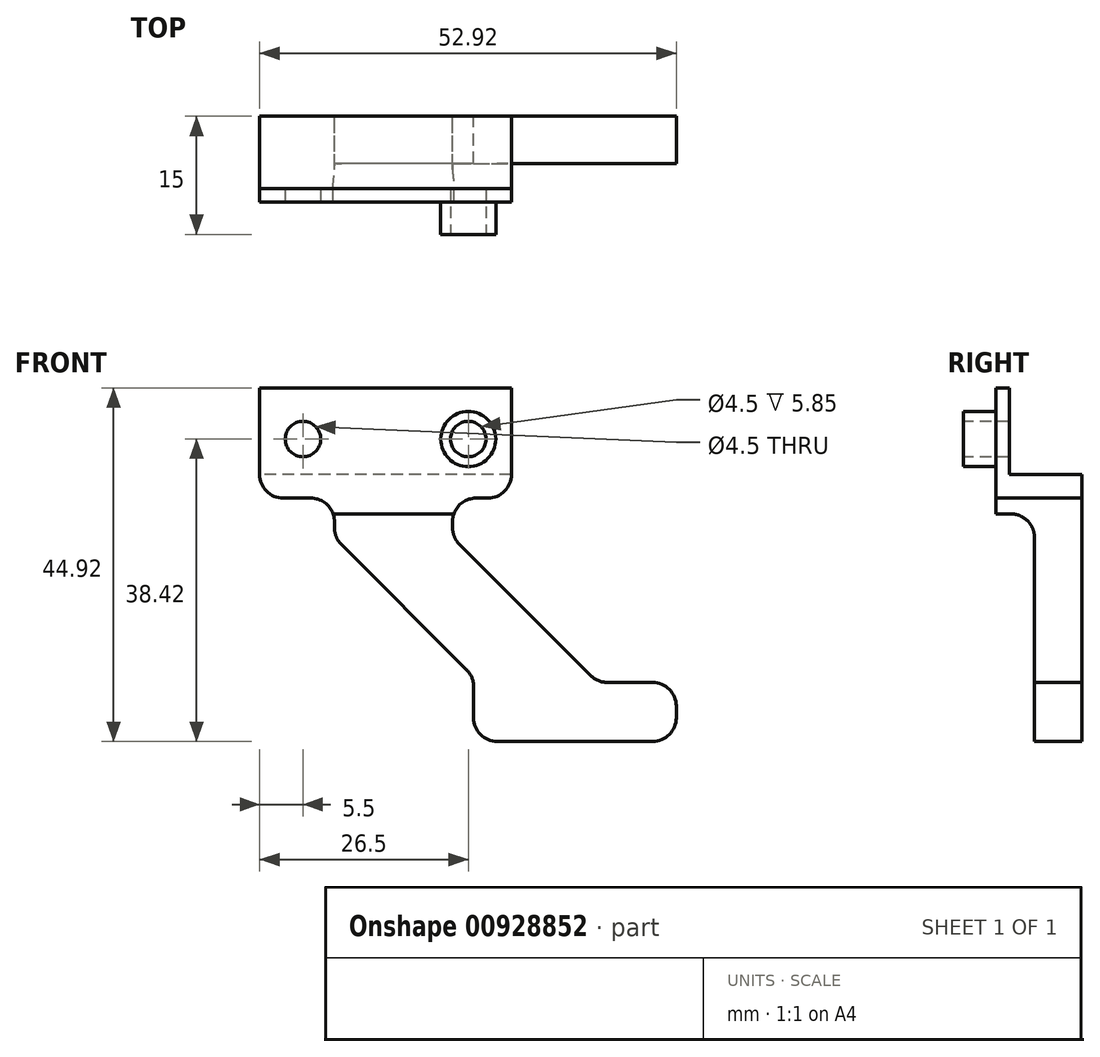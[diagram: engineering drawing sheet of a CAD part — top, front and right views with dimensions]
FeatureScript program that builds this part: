
annotation { "Feature Type Name" : "Feature", "Feature Type Description" : "" }
export const myFeature = defineFeature(function(context is Context, id is Id, definition is map)
    precondition{}
    {
        {
            var Q0;
            Q0=qCreatedBy(makeId("Front.planeOp"),FACE);
            var sketch = newSketch(context, id + "F0", { "sketchPlane" : qUnion([Q0])});
            skLineSegment(sketch, "E0", {"start": v(0, 0) * mm, "end": v(32, 0) * mm});
            skLineSegment(sketch, "E1", {"start": v(32, 0) * mm, "end": v(32, -11) * mm});
            skLineSegment(sketch, "E2", {"start": v(29, -14) * mm, "end": v(27.5, -14) * mm});
            skLineSegment(sketch, "E3", {"start": v(24.5, -17) * mm, "end": v(24.5, -17.76) * mm});
            skLineSegment(sketch, "E4", {"start": v(25.38, -19.88) * mm, "end": v(42.04, -36.54) * mm});
            skLineSegment(sketch, "E5", {"start": v(26.3, -35.8) * mm, "end": v(10.38, -19.88) * mm});
            skLineSegment(sketch, "E6", {"start": v(9.5, -17.76) * mm, "end": v(9.5, -17) * mm});
            skLineSegment(sketch, "E7", {"start": v(6.5, -14) * mm, "end": v(3, -14) * mm});
            skLineSegment(sketch, "E8", {"start": v(0, -11) * mm, "end": v(0, 0) * mm});
            skLineSegment(sketch, "E9", {"start": v(44.16, -37.42) * mm, "end": v(49.92, -37.42) * mm});
            skLineSegment(sketch, "E10", {"start": v(52.92, -40.42) * mm, "end": v(52.92, -41.92) * mm});
            skLineSegment(sketch, "E11", {"start": v(49.92, -44.92) * mm, "end": v(30.18, -44.92) * mm});
            skLineSegment(sketch, "E12", {"start": v(27.18, -41.92) * mm, "end": v(27.18, -37.92) * mm});
            skPoint(sketch, "E13.visualSharp", {"position": v(32, -14) * mm});
            skArc(sketch, "E13.filletArc", {"start": v(29, -14) * mm, "mid": v(31.12, -13.12) * mm, "end": v(32, -11) * mm});
            skPoint(sketch, "E14.visualSharp", {"position": v(24.5, -14) * mm});
            skArc(sketch, "E14.filletArc", {"start": v(27.5, -14) * mm, "mid": v(25.38, -14.88) * mm, "end": v(24.5, -17) * mm});
            skPoint(sketch, "E15.visualSharp", {"position": v(24.5, -19) * mm});
            skArc(sketch, "E15.filletArc", {"start": v(24.5, -17.76) * mm, "mid": v(24.73, -18.9) * mm, "end": v(25.38, -19.88) * mm});
            skPoint(sketch, "E16.visualSharp", {"position": v(42.92, -37.42) * mm});
            skArc(sketch, "E16.filletArc", {"start": v(42.04, -36.54) * mm, "mid": v(43.01, -37.2) * mm, "end": v(44.16, -37.42) * mm});
            skPoint(sketch, "E17.visualSharp", {"position": v(52.92, -37.42) * mm});
            skArc(sketch, "E17.filletArc", {"start": v(52.92, -40.42) * mm, "mid": v(52.04, -38.3) * mm, "end": v(49.92, -37.42) * mm});
            skPoint(sketch, "E18.visualSharp", {"position": v(52.92, -44.92) * mm});
            skArc(sketch, "E18.filletArc", {"start": v(49.92, -44.92) * mm, "mid": v(52.04, -44.04) * mm, "end": v(52.92, -41.92) * mm});
            skPoint(sketch, "E19.visualSharp", {"position": v(27.18, -44.92) * mm});
            skArc(sketch, "E19.filletArc", {"start": v(27.18, -41.92) * mm, "mid": v(28.06, -44.04) * mm, "end": v(30.18, -44.92) * mm});
            skPoint(sketch, "E20.visualSharp", {"position": v(27.18, -36.68) * mm});
            skArc(sketch, "E20.filletArc", {"start": v(27.18, -37.92) * mm, "mid": v(26.95, -36.77) * mm, "end": v(26.3, -35.8) * mm});
            skPoint(sketch, "E21.visualSharp", {"position": v(9.5, -19) * mm});
            skArc(sketch, "E21.filletArc", {"start": v(9.5, -17.76) * mm, "mid": v(9.73, -18.9) * mm, "end": v(10.38, -19.88) * mm});
            skPoint(sketch, "E22.visualSharp", {"position": v(9.5, -14) * mm});
            skArc(sketch, "E22.filletArc", {"start": v(9.5, -17) * mm, "mid": v(8.62, -14.88) * mm, "end": v(6.5, -14) * mm});
            skPoint(sketch, "E23.visualSharp", {"position": v(0, -14) * mm});
            skArc(sketch, "E23.filletArc", {"start": v(0, -11) * mm, "mid": v(0.88, -13.12) * mm, "end": v(3, -14) * mm});
            skSolve(sketch);
        }
        {
            var Q0;
            Q0 = qSketchRegion(id + "F0", true);
            extrude(context, id + "F1", {"entities" : qUnion([Q0]), "depth" : 15 * mm, "offsetDistance" : 25 * mm});
        }
        {
            var Q0;
            Q0=makeQuery(id+"F1.opExtrude","CAP_FACE",FACE,{"disambiguationData":[OSD([sQuery(id+"F0.wireOp",EDGE,"E0"),sQuery(id+"F0.wireOp",EDGE,"E1"),sQuery(id+"F0.wireOp",EDGE,"E2"),sQuery(id+"F0.wireOp",EDGE,"E3"),sQuery(id+"F0.wireOp",EDGE,"E4"),sQuery(id+"F0.wireOp",EDGE,"E5"),sQuery(id+"F0.wireOp",EDGE,"E6"),sQuery(id+"F0.wireOp",EDGE,"E7"),sQuery(id+"F0.wireOp",EDGE,"E8"),sQuery(id+"F0.wireOp",EDGE,"E9"),sQuery(id+"F0.wireOp",EDGE,"E10"),sQuery(id+"F0.wireOp",EDGE,"E11"),sQuery(id+"F0.wireOp",EDGE,"E12"),sQuery(id+"F0.wireOp",EDGE,"E13.filletArc"),sQuery(id+"F0.wireOp",EDGE,"E14.filletArc"),sQuery(id+"F0.wireOp",EDGE,"E15.filletArc"),sQuery(id+"F0.wireOp",EDGE,"E16.filletArc"),sQuery(id+"F0.wireOp",EDGE,"E17.filletArc"),sQuery(id+"F0.wireOp",EDGE,"E18.filletArc"),sQuery(id+"F0.wireOp",EDGE,"E19.filletArc"),sQuery(id+"F0.wireOp",EDGE,"E20.filletArc"),sQuery(id+"F0.wireOp",EDGE,"E21.filletArc"),sQuery(id+"F0.wireOp",EDGE,"E22.filletArc"),sQuery(id+"F0.wireOp",EDGE,"E23.filletArc")])],"isStart":false});
            var sketch = newSketch(context, id + "F2", { "sketchPlane" : qUnion([Q0])});
            skLineSegment(sketch, "E24", {"start": v(0, 0) * mm, "end": v(32, 0) * mm, "construction": true});
            skLineSegment(sketch, "E25", {"start": v(32, 0) * mm, "end": v(32, -14) * mm, "construction": true});
            skLineSegment(sketch, "E26", {"start": v(32, -14) * mm, "end": v(0, -14) * mm, "construction": true});
            skLineSegment(sketch, "E27", {"start": v(0, -14) * mm, "end": v(0, 0) * mm, "construction": true});
            skLineSegment(sketch, "E28", {"start": v(0, -6.5) * mm, "end": v(32, -6.5) * mm, "construction": true});
            skCircle(sketch, "E29", {"center": v(5.5, -6.5) * mm, "radius": 3.5 * mm});
            skLineSegment(sketch, "E30", {"start": v(16, 0) * mm, "end": v(16, -14) * mm, "construction": true});
            skCircle(sketch, "E31.MirrorC", {"center": v(26.5, -6.5) * mm, "radius": 3.5 * mm});
            skSolve(sketch);
        }
        {
            var Q0;
            Q0=makeQuery(id+"F2.imprint","IMPRINT",FACE,{"disambiguationData":[TD([[makeQuery(id+"F2.imprint","IMPRINT",EDGE,{"derivedFrom":sQuery(id+"F2.wireOp",EDGE,"E31.MirrorC")}),-1.0]])]});
            var Q1;
            Q1=makeQuery(id+"F2.imprint","IMPRINT",FACE,{"disambiguationData":[TD([[makeQuery(id+"F2.imprint","IMPRINT",EDGE,{"derivedFrom":sQuery(id+"F2.wireOp",EDGE,"E29")}),1.0]])]});
            extrude(context, id + "F3", {"entities" : qUnion([Q0, Q1]), "operationType" : NewBodyOperationType.REMOVE, "oppositeDirection" : true, "depth" : 4.1 * mm, "offsetDistance" : 25 * mm});
        }
        {
            var Q0;
            Q0=makeQuery(id+"F1.opExtrude","CAP_FACE",FACE,{"disambiguationData":[OSD([sQuery(id+"F0.wireOp",EDGE,"E0"),sQuery(id+"F0.wireOp",EDGE,"E1"),sQuery(id+"F0.wireOp",EDGE,"E2"),sQuery(id+"F0.wireOp",EDGE,"E3"),sQuery(id+"F0.wireOp",EDGE,"E4"),sQuery(id+"F0.wireOp",EDGE,"E5"),sQuery(id+"F0.wireOp",EDGE,"E6"),sQuery(id+"F0.wireOp",EDGE,"E7"),sQuery(id+"F0.wireOp",EDGE,"E8"),sQuery(id+"F0.wireOp",EDGE,"E9"),sQuery(id+"F0.wireOp",EDGE,"E10"),sQuery(id+"F0.wireOp",EDGE,"E11"),sQuery(id+"F0.wireOp",EDGE,"E12"),sQuery(id+"F0.wireOp",EDGE,"E13.filletArc"),sQuery(id+"F0.wireOp",EDGE,"E14.filletArc"),sQuery(id+"F0.wireOp",EDGE,"E15.filletArc"),sQuery(id+"F0.wireOp",EDGE,"E16.filletArc"),sQuery(id+"F0.wireOp",EDGE,"E17.filletArc"),sQuery(id+"F0.wireOp",EDGE,"E18.filletArc"),sQuery(id+"F0.wireOp",EDGE,"E19.filletArc"),sQuery(id+"F0.wireOp",EDGE,"E20.filletArc"),sQuery(id+"F0.wireOp",EDGE,"E21.filletArc"),sQuery(id+"F0.wireOp",EDGE,"E22.filletArc"),sQuery(id+"F0.wireOp",EDGE,"E23.filletArc")])],"isStart":false});
            var sketch = newSketch(context, id + "F4", { "sketchPlane" : qUnion([Q0])});
            skCircle(sketch, "E32", {"center": v(5.5, -6.5) * mm, "radius": 2.25 * mm});
            skCircle(sketch, "E33", {"center": v(26.5, -6.5) * mm, "radius": 2.25 * mm});
            skSolve(sketch);
        }
        {
            var Q0;
            Q0 = qSketchRegion(id + "F4", true);
            extrude(context, id + "F5", {"entities" : qUnion([Q0]), "operationType" : NewBodyOperationType.REMOVE, "oppositeDirection" : true, "depth" : 25 * mm, "offsetDistance" : 25 * mm});
        }
        {
            var Q0;
            Q0=makeQuery(id+"F1.opExtrude","SWEPT_FACE",FACE,{"disambiguationData":[OSD([sQuery(id+"F0.wireOp",EDGE,"E8")])]});
            var sketch = newSketch(context, id + "F6", { "sketchPlane" : qUnion([Q0])});
            skLineSegment(sketch, "E34.bottom", {"start": v(0, 0) * mm, "end": v(9.15, 0) * mm});
            skLineSegment(sketch, "E34.top", {"start": v(0, -11) * mm, "end": v(9.15, -11) * mm});
            skLineSegment(sketch, "E34.left", {"start": v(0, 0) * mm, "end": v(0, -11) * mm});
            skLineSegment(sketch, "E34.right", {"start": v(9.15, 0) * mm, "end": v(9.15, -11) * mm});
            skLineSegment(sketch, "E35.bottom", {"start": v(9, -48) * mm, "end": v(15, -48) * mm});
            skLineSegment(sketch, "E35.top", {"start": v(9, -16) * mm, "end": v(15, -16) * mm});
            skLineSegment(sketch, "E35.left", {"start": v(6, -45) * mm, "end": v(6, -19) * mm});
            skLineSegment(sketch, "E35.right", {"start": v(15, -48) * mm, "end": v(15, -16) * mm});
            skPoint(sketch, "E36.visualSharp", {"position": v(6, -16) * mm});
            skArc(sketch, "E36.filletArc", {"start": v(9, -16) * mm, "mid": v(6.88, -16.88) * mm, "end": v(6, -19) * mm});
            skPoint(sketch, "E37.visualSharp", {"position": v(6, -48) * mm});
            skArc(sketch, "E37.filletArc", {"start": v(6, -45) * mm, "mid": v(6.88, -47.12) * mm, "end": v(9, -48) * mm});
            skSolve(sketch);
        }
        {
            var Q0;
            Q0 = qSketchRegion(id + "F6", true);
            extrude(context, id + "F7", {"entities" : qUnion([Q0]), "operationType" : NewBodyOperationType.REMOVE, "endBound" : BoundingType.THROUGH_ALL, "oppositeDirection" : true, "depth" : 25 * mm, "offsetDistance" : 25 * mm});
        }
    });
